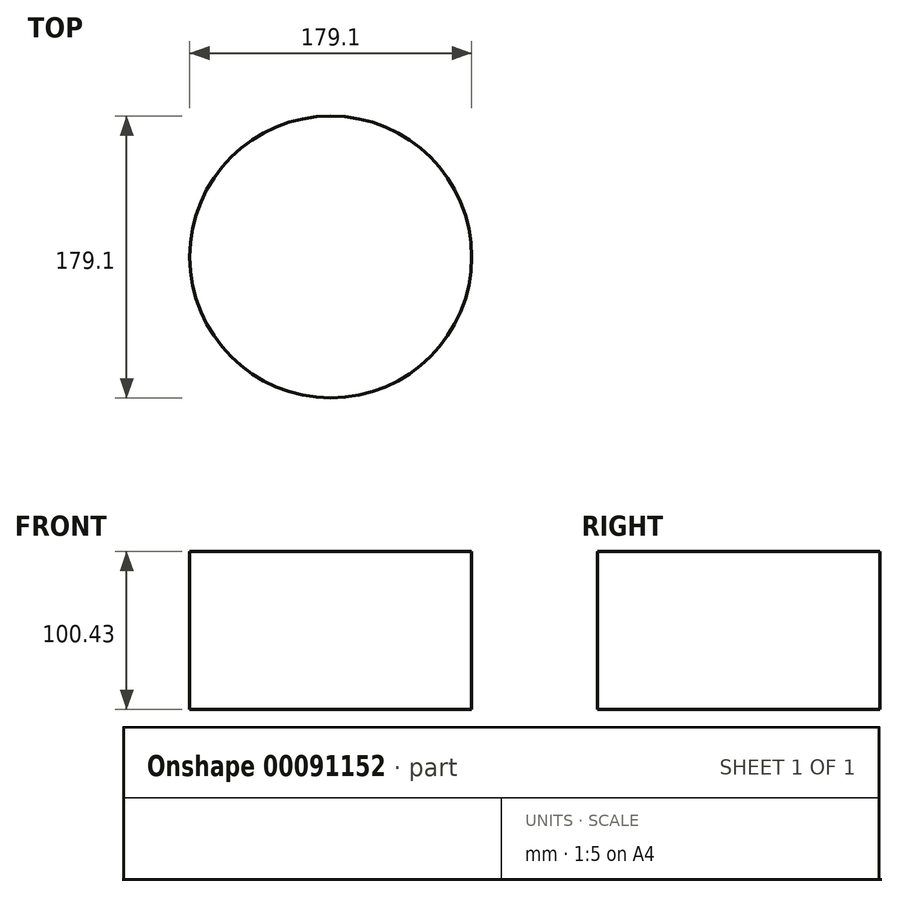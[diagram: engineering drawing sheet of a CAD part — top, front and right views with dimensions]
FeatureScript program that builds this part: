
annotation { "Feature Type Name" : "Feature", "Feature Type Description" : "" }
export const myFeature = defineFeature(function(context is Context, id is Id, definition is map)
    precondition{}
    {
        {
            var Q0;
            Q0=qCreatedBy(makeId("Top.planeOp"),FACE);
            var sketch = newSketch(context, id + "F0", { "sketchPlane" : qUnion([Q0])});
            skCircle(sketch, "E0", {"center": v(0, 0) * mm, "radius": 93.95 * mm});
            skSolve(sketch);
        }
        {
            var Q0;
            Q0=makeQuery(id+"F0.imprint","IMPRINT",FACE,{"disambiguationData":[TD([[makeQuery(id+"F0.imprint","IMPRINT",EDGE,{"derivedFrom":sQuery(id+"F0.wireOp",EDGE,"E0")}),1.0]])]});
            extrude(context, id + "F1", {"entities" : qUnion([Q0]), "depth" : 381 * mm});
        }
        {
            var Q0;
            Q0=makeQuery(id+"F1.opExtrude","CAP_FACE",FACE,{"disambiguationData":[OSD([sQuery(id+"F0.wireOp",EDGE,"E0")])],"isStart":false});
            extrude(context, id + "F2", {"entities" : qUnion([Q0]), "operationType" : NewBodyOperationType.REMOVE, "oppositeDirection" : true, "depth" : 76.2 * mm});
        }
        {
            var Q0;
            Q0=makeQuery(id+"F1.opExtrude","CAP_FACE",FACE,{"disambiguationData":[OSD([sQuery(id+"F0.wireOp",EDGE,"E0")])],"isStart":true});
            var sketch = newSketch(context, id + "F3", { "sketchPlane" : qUnion([Q0])});
            skCircle(sketch, "E1", {"center": v(0, 0) * mm, "radius": 89.55 * mm});
            skSolve(sketch);
        }
        {
            var Q0;
            Q0=makeQuery(id+"F3.imprint","IMPRINT",FACE,{"disambiguationData":[TD([[makeQuery(id+"F3.imprint","IMPRINT",EDGE,{"derivedFrom":sQuery(id+"F3.wireOp",EDGE,"E1")}),1.0]])]});
            extrude(context, id + "F4", {"entities" : qUnion([Q0]), "operationType" : NewBodyOperationType.INTERSECT, "oppositeDirection" : true, "depth" : 100.43 * mm});
        }
    });
